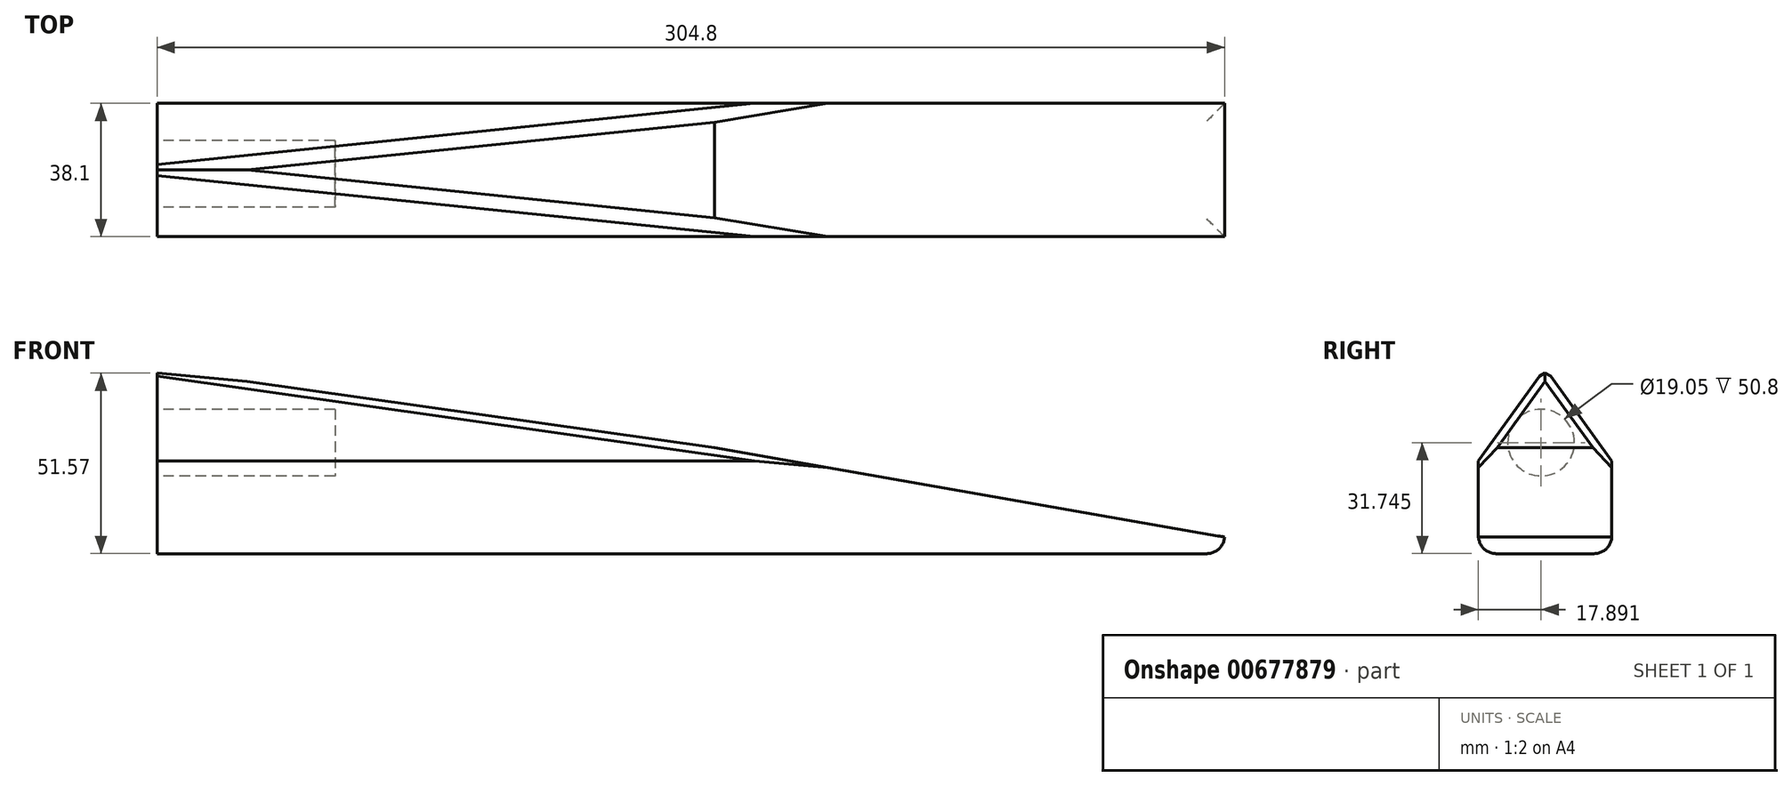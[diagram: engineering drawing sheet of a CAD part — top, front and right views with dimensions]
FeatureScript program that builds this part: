
annotation { "Feature Type Name" : "Feature", "Feature Type Description" : "" }
export const myFeature = defineFeature(function(context is Context, id is Id, definition is map)
    precondition{}
    {
        {
            var Q0;
            Q0=qCreatedBy(makeId("Front.planeOp"),FACE);
            var sketch = newSketch(context, id + "F0", { "sketchPlane" : qUnion([Q0])});
            skLineSegment(sketch, "E0", {"start": v(-114.43, 15.88) * mm, "end": v(190.37, 15.88) * mm});
            skLineSegment(sketch, "E1", {"start": v(-114.43, 15.88) * mm, "end": v(-114.43, 79.38) * mm});
            skLineSegment(sketch, "E2", {"start": v(190.37, 15.88) * mm, "end": v(190.37, 34.93) * mm});
            skLineSegment(sketch, "E3", {"start": v(-114.43, 79.38) * mm, "end": v(190.37, 34.93) * mm});
            skSolve(sketch);
        }
        {
            var Q0;
            Q0=makeQuery(id+"F0.imprint","IMPRINT",FACE,{"disambiguationData":[TD([[makeQuery(id+"F0.imprint","IMPRINT",EDGE,{"derivedFrom":sQuery(id+"F0.wireOp",EDGE,"E0")}),1.0]])]});
            extrude(context, id + "F1", {"entities" : qUnion([Q0]), "depth" : 38.1 * mm, "offsetDistance" : 25.4 * mm});
        }
        {
            var Q0;
            Q0=makeQuery(id+"F1.opExtrude","SWEPT_FACE",FACE,{"disambiguationData":[OSD([sQuery(id+"F0.wireOp",EDGE,"E1")])]});
            var sketch = newSketch(context, id + "F2", { "sketchPlane" : qUnion([Q0])});
            skCircle(sketch, "E4", {"center": v(20.2, 47.63) * mm, "radius": 9.53 * mm});
            skPoint(sketch, "E4.centerSnap0", {"position": v(38.1, 47.63) * mm});
            skSolve(sketch);
        }
        {
            var Q0;
            Q0=makeQuery(id+"F2.imprint","IMPRINT",FACE,{"disambiguationData":[TD([[makeQuery(id+"F2.imprint","IMPRINT",EDGE,{"derivedFrom":sQuery(id+"F2.wireOp",EDGE,"E4")}),1.0]])]});
            extrude(context, id + "F3", {"entities" : qUnion([Q0]), "operationType" : NewBodyOperationType.REMOVE, "oppositeDirection" : true, "depth" : 50.8 * mm, "offsetDistance" : 25.4 * mm});
        }
        {
            var Q0;
            Q0=makeQuery(id+"F1.opExtrude","CAP_FACE",FACE,{"disambiguationData":[OSD([sQuery(id+"F0.wireOp",EDGE,"E0"),sQuery(id+"F0.wireOp",EDGE,"E1"),sQuery(id+"F0.wireOp",EDGE,"E2"),sQuery(id+"F0.wireOp",EDGE,"E3")])],"isStart":false});
            var sketch = newSketch(context, id + "F4", { "sketchPlane" : qUnion([Q0])});
            skLineSegment(sketch, "E5.0.0", {"start": v(190.37, 34.93) * mm, "end": v(-114.43, 79.38) * mm});
            skLineSegment(sketch, "E5.0.1", {"start": v(-114.43, 79.38) * mm, "end": v(-114.43, 15.88) * mm});
            skLineSegment(sketch, "E5.0.2", {"start": v(-114.43, 15.88) * mm, "end": v(190.37, 15.88) * mm});
            skLineSegment(sketch, "E5.0.3", {"start": v(190.37, 15.88) * mm, "end": v(190.37, 34.93) * mm});
            skLineSegment(sketch, "E6", {"start": v(190.37, 25.4) * mm, "end": v(-114.43, 68.81) * mm});
            skSolve(sketch);
        }
        {
            var Q0;
            {var subQ0=sQuery(id+"F4.wireOp",EDGE,"E5.0.0");Q0=makeQuery(id+"F4.imprint","IMPRINT",FACE,{"disambiguationData":[TD([[makeQuery(id+"F4.imprint","IMPRINT",EDGE,{"derivedFrom":subQ0}),-1.0]])]});}
            extrude(context, id + "F5", {"entities" : qUnion([Q0]), "operationType" : NewBodyOperationType.REMOVE, "oppositeDirection" : true, "depth" : 38.1 * mm, "offsetDistance" : 25.4 * mm});
        }
        {
            var Q0;
            Q0=makeQuery(id+"F1.opExtrude","CAP_FACE",FACE,{"disambiguationData":[OSD([sQuery(id+"F0.wireOp",EDGE,"E0"),sQuery(id+"F0.wireOp",EDGE,"E1"),sQuery(id+"F0.wireOp",EDGE,"E2"),sQuery(id+"F0.wireOp",EDGE,"E3")])],"isStart":false});
            var sketch = newSketch(context, id + "F6", { "sketchPlane" : qUnion([Q0])});
            skLineSegment(sketch, "E7", {"start": v(190.37, 20.64) * mm, "end": v(44.72, 46.15) * mm});
            skSolve(sketch);
        }
        {
            var Q0;
            {var subQ0=sQuery(id+"F6.wireOp",EDGE,"E7");Q0=makeQuery(id+"F6.imprint","IMPRINT",FACE,{"disambiguationData":[TD([[makeQuery(id+"F6.imprint","IMPRINT",EDGE,{"derivedFrom":subQ0}),-1.0]])]});}
            extrude(context, id + "F7", {"entities" : qUnion([Q0]), "operationType" : NewBodyOperationType.REMOVE, "oppositeDirection" : true, "depth" : 38.1 * mm, "offsetDistance" : 25.4 * mm});
        }
        {
            var Q0;
            Q0=makeQuery(id+"F1.opExtrude","SWEPT_FACE",FACE,{"disambiguationData":[OSD([sQuery(id+"F0.wireOp",EDGE,"E1")])]});
            var sketch = newSketch(context, id + "F8", { "sketchPlane" : qUnion([Q0])});
            skLineSegment(sketch, "E8", {"start": v(0, 42.34) * mm, "end": v(19.05, 68.81) * mm});
            skLineSegment(sketch, "E9", {"start": v(19.05, 68.81) * mm, "end": v(38.1, 42.34) * mm});
            skSolve(sketch);
        }
        {
            var Q0;
            {var subQ0=sQuery(id+"F8.wireOp",EDGE,"E8");Q0=makeQuery(id+"F8.imprint","IMPRINT",FACE,{"disambiguationData":[TD([[makeQuery(id+"F8.imprint","IMPRINT",EDGE,{"derivedFrom":subQ0}),1.0]])]});}
            var Q1;
            {var subQ0=sQuery(id+"F8.wireOp",EDGE,"E9");Q1=makeQuery(id+"F8.imprint","IMPRINT",FACE,{"disambiguationData":[TD([[makeQuery(id+"F8.imprint","IMPRINT",EDGE,{"derivedFrom":subQ0}),1.0]])]});}
            extrude(context, id + "F9", {"entities" : qUnion([Q0, Q1]), "operationType" : NewBodyOperationType.REMOVE, "oppositeDirection" : true, "depth" : 254 * mm, "offsetDistance" : 25.4 * mm});
        }
        {
            var Q0;
            Q0=makeQuery(id+"F9.boolean.opBoolean","INTERSECT",EDGE,{"derivedFrom":[makeQuery(id+"F5.boolean.opBoolean","COPY",FACE,{"derivedFrom":makeQuery(id+"F5.opExtrude","SWEPT_FACE",FACE,{"disambiguationData":[OSD([sQuery(id+"F4.wireOp",EDGE,"E6")])]})}),makeQuery(id+"F9.opExtrude","SWEPT_FACE",FACE,{"disambiguationData":[OSD([sQuery(id+"F8.wireOp",EDGE,"E8")])]})]});
            var Q1;
            Q1=makeQuery(id+"F9.boolean.opBoolean","INTERSECT",EDGE,{"derivedFrom":[makeQuery(id+"F5.boolean.opBoolean","COPY",FACE,{"derivedFrom":makeQuery(id+"F5.opExtrude","SWEPT_FACE",FACE,{"disambiguationData":[OSD([sQuery(id+"F4.wireOp",EDGE,"E6")])]})}),makeQuery(id+"F9.opExtrude","SWEPT_FACE",FACE,{"disambiguationData":[OSD([sQuery(id+"F8.wireOp",EDGE,"E9")])]})]});
            var Q2;
            Q2=makeQuery(id+"F7.boolean.opBoolean","COPY",EDGE,{"derivedFrom":makeQuery(id+"F7.opExtrude","CAP_EDGE",EDGE,{"disambiguationData":[OSD([sQuery(id+"F6.wireOp",EDGE,"E7")])],"isStart":false})});
            var Q3;
            Q3=makeQuery(id+"F7.boolean.opBoolean","COPY",EDGE,{"derivedFrom":makeQuery(id+"F7.opExtrude","CAP_EDGE",EDGE,{"disambiguationData":[OSD([sQuery(id+"F6.wireOp",EDGE,"E7")])],"isStart":true})});
            chamfer(context, id + "F10", {"entities" : qUnion([Q0, Q1, Q2, Q3]), "width" : 5.08 * mm, "tangentPropagation" : true});
        }
        {
            var Q0;
            Q0=makeQuery(id+"F9.boolean.opBoolean","COPY",EDGE,{"derivedFrom":makeQuery(id+"F9.opExtrude","SWEPT_EDGE",EDGE,{"disambiguationData":[OSD([sQuery(id+"F0.wireOp",EDGE,"E1"),sQuery(id+"F8.wireOp",EDGE,"E9")])]})});
            var Q1;
            Q1=makeQuery(id+"F9.boolean.opBoolean","COPY",EDGE,{"derivedFrom":makeQuery(id+"F9.opExtrude","SWEPT_EDGE",EDGE,{"disambiguationData":[OSD([sQuery(id+"F0.wireOp",EDGE,"E1"),sQuery(id+"F8.wireOp",EDGE,"E8")])]})});
            var Q2;
            Q2=makeQuery(id+"F1.opExtrude","SWEPT_EDGE",EDGE,{"disambiguationData":[OSD([sQuery(id+"F0.wireOp",EDGE,"E0"),sQuery(id+"F0.wireOp",EDGE,"E2")])]});
            var Q3;
            Q3=makeQuery(id+"F10.opChamfer","BLEND_EDGE",EDGE,{"blendedFrom":[makeQuery(id+"F7.boolean.opBoolean","COPY",EDGE,{"derivedFrom":makeQuery(id+"F7.opExtrude","CAP_EDGE",EDGE,{"disambiguationData":[OSD([sQuery(id+"F6.wireOp",EDGE,"E7")])],"isStart":true})}),makeQuery(id+"F1.opExtrude","CAP_FACE",FACE,{"disambiguationData":[OSD([sQuery(id+"F0.wireOp",EDGE,"E0"),sQuery(id+"F0.wireOp",EDGE,"E1"),sQuery(id+"F0.wireOp",EDGE,"E2"),sQuery(id+"F0.wireOp",EDGE,"E3")])],"isStart":false})],"blendedInto":[makeQuery(id+"F1.opExtrude","CAP_FACE",FACE,{"disambiguationData":[OSD([sQuery(id+"F0.wireOp",EDGE,"E0"),sQuery(id+"F0.wireOp",EDGE,"E1"),sQuery(id+"F0.wireOp",EDGE,"E2"),sQuery(id+"F0.wireOp",EDGE,"E3")])],"isStart":false})]});
            var Q4;
            Q4=makeQuery(id+"F10.opChamfer","BLEND_EDGE",EDGE,{"blendedFrom":[makeQuery(id+"F7.boolean.opBoolean","COPY",EDGE,{"derivedFrom":makeQuery(id+"F7.opExtrude","CAP_EDGE",EDGE,{"disambiguationData":[OSD([sQuery(id+"F6.wireOp",EDGE,"E7")])],"isStart":false})}),makeQuery(id+"F1.opExtrude","CAP_FACE",FACE,{"disambiguationData":[OSD([sQuery(id+"F0.wireOp",EDGE,"E0"),sQuery(id+"F0.wireOp",EDGE,"E1"),sQuery(id+"F0.wireOp",EDGE,"E2"),sQuery(id+"F0.wireOp",EDGE,"E3")])],"isStart":true})],"blendedInto":[makeQuery(id+"F1.opExtrude","CAP_FACE",FACE,{"disambiguationData":[OSD([sQuery(id+"F0.wireOp",EDGE,"E0"),sQuery(id+"F0.wireOp",EDGE,"E1"),sQuery(id+"F0.wireOp",EDGE,"E2"),sQuery(id+"F0.wireOp",EDGE,"E3")])],"isStart":true})]});
            var Q5;
            Q5=makeQuery(id+"F1.opExtrude","CAP_EDGE",EDGE,{"disambiguationData":[OSD([sQuery(id+"F0.wireOp",EDGE,"E0")])],"isStart":false});
            var Q6;
            Q6=makeQuery(id+"F1.opExtrude","CAP_EDGE",EDGE,{"disambiguationData":[OSD([sQuery(id+"F0.wireOp",EDGE,"E0")])],"isStart":true});
            fillet(context, id + "F11", {"entities" : qUnion([Q0, Q1, Q2, Q3, Q4, Q5, Q6]), "radius" : 5.08 * mm, "tangentPropagation" : true, "allowEdgeOverflow" : false});
        }
    });
